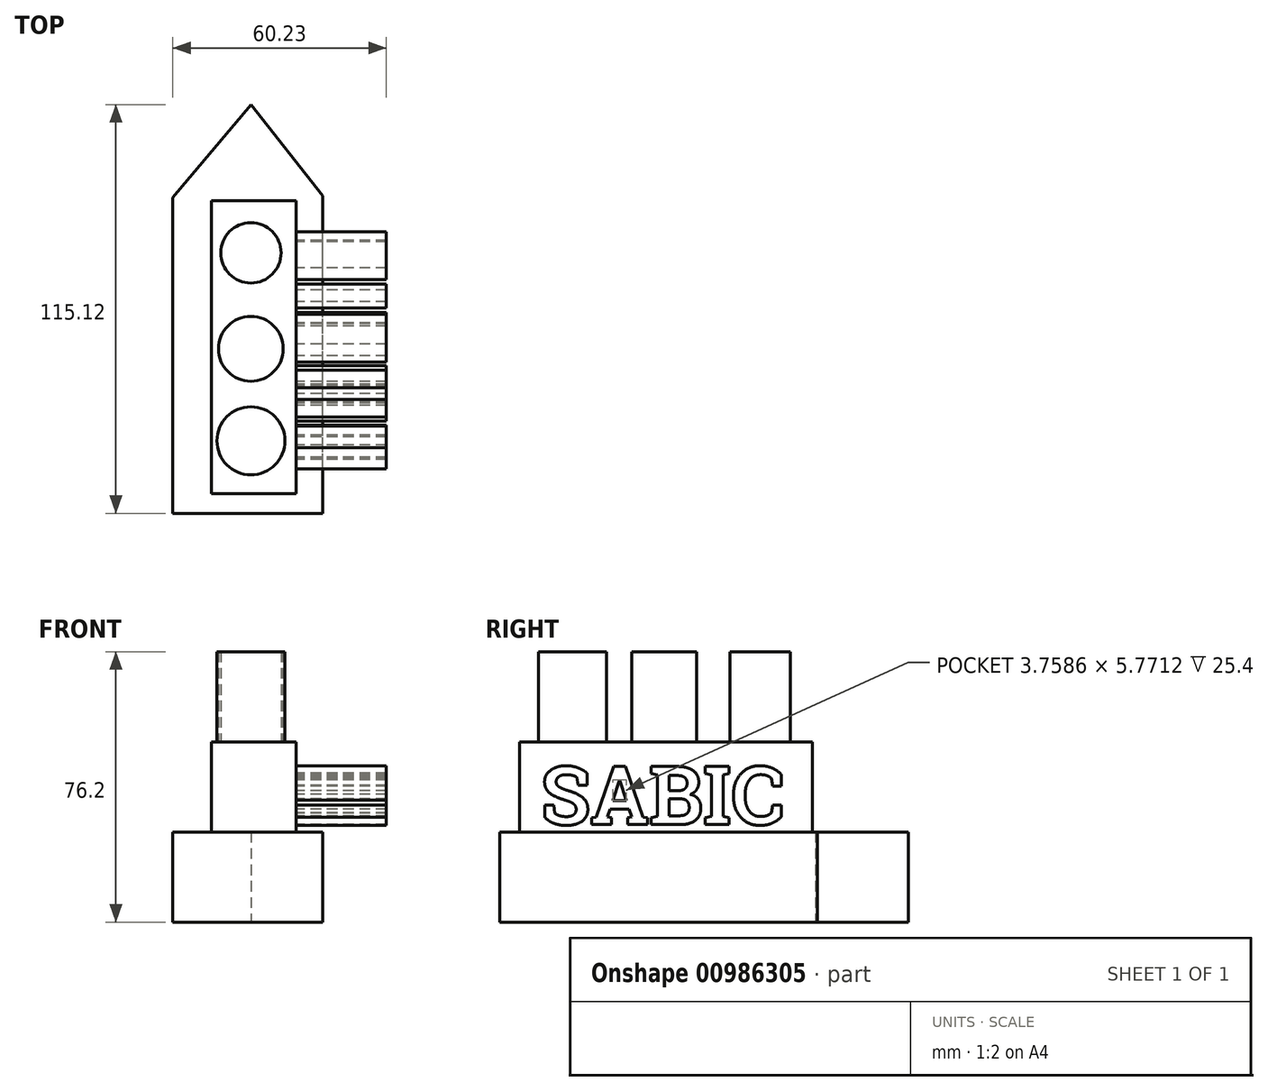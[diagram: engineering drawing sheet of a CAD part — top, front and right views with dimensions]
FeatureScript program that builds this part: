
annotation { "Feature Type Name" : "Feature", "Feature Type Description" : "" }
export const myFeature = defineFeature(function(context is Context, id is Id, definition is map)
    precondition{}
    {
        {
            var Q0;
            Q0=qCreatedBy(makeId("Top.planeOp"),FACE);
            var sketch = newSketch(context, id + "F0", { "sketchPlane" : qUnion([Q0])});
            skLineSegment(sketch, "E0", {"start": v(-22.02, 32.95) * mm, "end": v(-22.02, -55.98) * mm});
            skLineSegment(sketch, "E1", {"start": v(-22.02, -55.98) * mm, "end": v(20.3, -55.98) * mm});
            skLineSegment(sketch, "E2", {"start": v(20.3, -55.98) * mm, "end": v(20.3, 33.53) * mm});
            skLineSegment(sketch, "E3", {"start": v(20.3, 33.53) * mm, "end": v(0, 59.14) * mm});
            skLineSegment(sketch, "E4", {"start": v(0, 59.14) * mm, "end": v(-22.02, 32.95) * mm});
            skSolve(sketch);
        }
        {
            var Q0;
            Q0=makeQuery(id+"FgCUWMOuX6ASdoM_0.imprint","IMPRINT",FACE,{"disambiguationData":[TD([[makeQuery(id+"FgCUWMOuX6ASdoM_0.imprint","IMPRINT",EDGE,{"derivedFrom":sQuery(id+"FgCUWMOuX6ASdoM_0.wireOp",EDGE,"TtBqpdve-JNVj-KW5h-tHQa-nymekkQrzRrJ.bottom")}),-1.0]])]});
            var Q1;
            Q1 = qSketchRegion(id + "F0", true);
            extrude(context, id + "F1", {"entities" : qUnion([Q0, Q1]), "depth" : 25.4 * mm, "offsetDistance" : 25.4 * mm});
        }
        {
            var Q0;
            Q0=makeQuery(id+"F1.opExtrude","CAP_FACE",FACE,{"disambiguationData":[OSD([sQuery(id+"F0.wireOp",EDGE,"E0"),sQuery(id+"F0.wireOp",EDGE,"E1"),sQuery(id+"F0.wireOp",EDGE,"E2"),sQuery(id+"F0.wireOp",EDGE,"E3"),sQuery(id+"F0.wireOp",EDGE,"E4")])],"isStart":false});
            var sketch = newSketch(context, id + "F2", { "sketchPlane" : qUnion([Q0])});
            skLineSegment(sketch, "E5.bottom", {"start": v(-11.08, 32.1) * mm, "end": v(12.8, 32.1) * mm});
            skLineSegment(sketch, "E5.top", {"start": v(-11.08, -50.5) * mm, "end": v(12.8, -50.5) * mm});
            skLineSegment(sketch, "E5.left", {"start": v(-11.08, 32.1) * mm, "end": v(-11.08, -50.5) * mm});
            skLineSegment(sketch, "E5.right", {"start": v(12.8, 32.1) * mm, "end": v(12.8, -50.5) * mm});
            skSolve(sketch);
        }
        {
            var Q0;
            Q0 = qSketchRegion(id + "F2", true);
            extrude(context, id + "F3", {"entities" : qUnion([Q0]), "operationType" : NewBodyOperationType.ADD, "depth" : 25.4 * mm, "offsetDistance" : 25.4 * mm});
        }
        {
            var Q0;
            Q0=makeQuery(id+"F3.opExtrude","CAP_FACE",FACE,{"disambiguationData":[OSD([sQuery(id+"F2.wireOp",EDGE,"E5.bottom"),sQuery(id+"F2.wireOp",EDGE,"E5.top"),sQuery(id+"F2.wireOp",EDGE,"E5.left"),sQuery(id+"F2.wireOp",EDGE,"E5.right")])],"isStart":false});
            var sketch = newSketch(context, id + "F4", { "sketchPlane" : qUnion([Q0])});
            skCircle(sketch, "E6", {"center": v(0, 17.41) * mm, "radius": 8.51 * mm});
            skCircle(sketch, "E7", {"center": v(0, -9.64) * mm, "radius": 9.13 * mm});
            skCircle(sketch, "E8", {"center": v(0, -35.54) * mm, "radius": 9.59 * mm});
            skSolve(sketch);
        }
        {
            var Q0;
            Q0 = qSketchRegion(id + "F4", true);
            extrude(context, id + "F5", {"entities" : qUnion([Q0]), "operationType" : NewBodyOperationType.ADD, "depth" : 25.4 * mm, "offsetDistance" : 25.4 * mm});
        }
        {
            var Q0;
            Q0=makeQuery(id+"F3.opExtrude","SWEPT_FACE",FACE,{"disambiguationData":[OSD([sQuery(id+"F2.wireOp",EDGE,"E5.right")])]});
            var sketch = newSketch(context, id + "F6", { "sketchPlane" : qUnion([Q0])});
            skSolve(sketch);
        }
        {
            var Q0;
            {var subQ0=sQuery(id+"F2.wireOp",EDGE,"E5.right");Q0=makeQuery(id+"F6.imprint","IMPRINT",FACE,{"disambiguationData":[TD([[makeQuery(id+"F6.imprint","IMPRINT",EDGE,{"derivedFrom":makeQuery(id+"F3.opExtrude","CAP_EDGE",EDGE,{"disambiguationData":[OSD([subQ0])],"isStart":false})}),1.0]])]});}
            var sketch = newSketch(context, id + "F7", { "sketchPlane" : qUnion([Q0])});
            skText(sketch, "E9", { "text": "SABIC", "fontName": "RobotoSlab-Bold.ttf"});
            const initialGuessF7  = {"E9": [-0.0445, 0.02746, 1, 0, 0.01659]};
            skSetInitialGuess(sketch, initialGuessF7);
            skSolve(sketch);
        }
        {
            var Q0;
            Q0 = qSketchRegion(id + "F7", true);
            extrude(context, id + "F8", {"entities" : qUnion([Q0]), "operationType" : NewBodyOperationType.ADD, "depth" : 25.4 * mm, "offsetDistance" : 25.4 * mm});
        }
    });
